# Revit family: Plumbing-Fix_Soap-Disp-Touchless_Stern_Trendy
name_source: partatom
category: Plumbing Fixtures
revit_build: Autodesk Revit 2015 (Build: 20140606_1530(x64)
units: mm (PartAtom-declared; Revit-internal decimal feet)

## types (8) — shared parameters
Assembly Code = D2010300
Available Options = as Specified
CW Connection = No
Default Elevation = 0' - 0"
HW Connection = No
Link to Related Files = https://www.arcat.com
Manufacturer = Stern Engineering
Manufacturer Website = http://www.sternfaucets.com
Product Data = http://www.arcat.com
Revision = R1_2018-04
Sales Information = http://www.sternfaucets.com
Spout Height = 0' - 2 7/8"
Spout Reach = 0' - 3 1/8"
Standards Conformance = as Specified
Type Comments = as Specified
URL = http://www.sternfaucets.com
Unit Height = 0' - 4 1/8"
Unit Width = 0' - 1 3/4"
Vent Connection = No
Warranty Duration (Years) = 2
Waste Connection = No
zero-valued in all types: CWFU, Cost, Expected Lifespan (Years), HWFU, Maintenance Schedule (Months), WFU

## per-type parameters (varying)
| type | Capacity | Description | Include MF Pump | Model | Power Supply | Product Features |
| Standard Battery Pack | 33 oz / 1 liter Liquid | Stern Touchless Deck Mounted Soap Dispenser - Trendy Soap Dispenser B as Specified | No | Trendy Soap Dispenser B | 6x DD Batteries | as Specified |
| Standard Transformer | 33 oz / 1 liter Liquid | Stern Touchless Deck Mounted Soap Dispenser - Trendy Soap Dispenser E as Specified | No | Trendy Soap Dispenser E | 12V Transformer | as Specified |
| Standard Foam | 33 oz / 1 liter Foam | Stern Touchless Deck Mounted Foam Soap Dispenser - Trendy Foam E as Specified | No | Trendy Foam E | 12V Transformer | as Specified |
| AISI316 Standard Transformer | 33 oz / 1 liter Liquid | Stern Touchless Deck Mounted Soap Dispenser - Trendy Soap Dispenser E AISI316 as Specified | No | Trendy Soap Dispenser E AISI316 | 12V Transformer | AISI316 Body |
| AISI316 Standard Foam | 33 oz / 1 liter Foam | Stern Touchless Deck Mounted Foam Soap Dispenser - Trendy Foam E AISI316 as Specified | No | Trendy Foam E AISI316 | 12V Transformer | AISI316 Body |
| Multifeed Liquid | as Specified | Stern Touchless Deck Mounted Soap Dispenser - MF Trendy Soap Dispenser as Specified | Yes | MF Trendy Soap Dispenser | 12V Transformer | as Specified |
| Multifeed Foam | as Specified | Stern Touchless Deck Mounted Foam Soap Dispenser - MF Trendy Foam Dispesnser as Specified | Yes | MF Trendy Foam Dispesnser | 12V Transformer | as Specified |
| SD 1.6 gal / 6 liters | 1.6 gal / 6 liters Liquid | Stern Touchless Deck Mounted Soap Dispenser - Trendy SD 1.6 E as Specified | Yes | Trendy SD 1.6 E | 12V Transformer | as Specified |

## geometry (parser evidence)
native form markers: Sweep x5
no freeform markers — native parametric forms only
